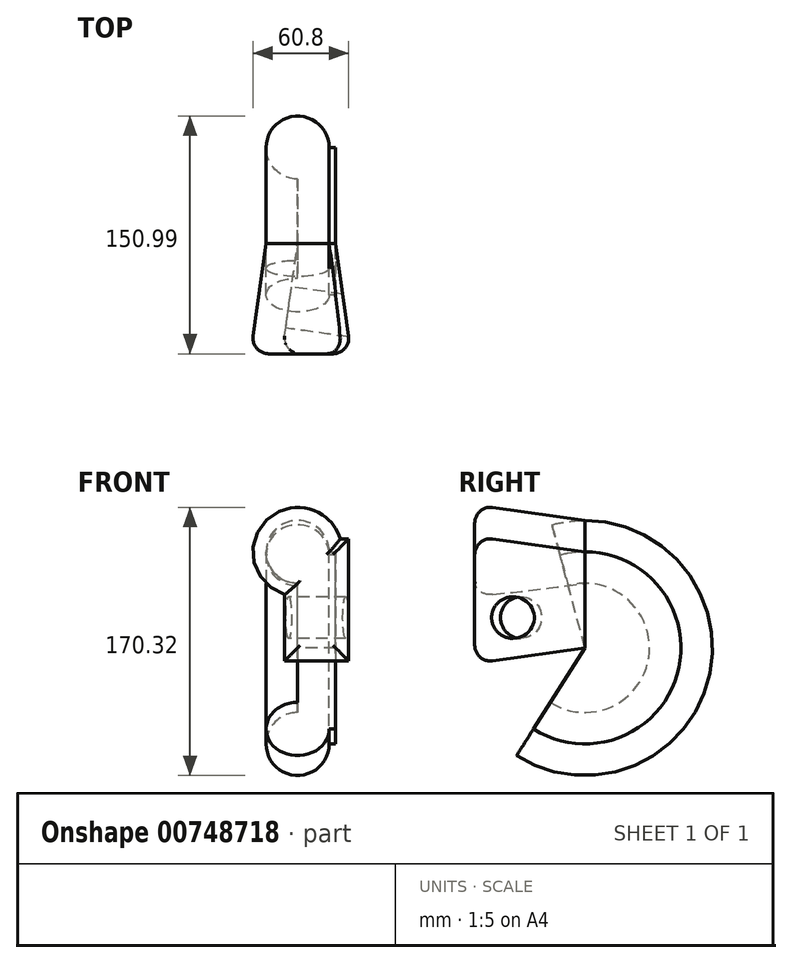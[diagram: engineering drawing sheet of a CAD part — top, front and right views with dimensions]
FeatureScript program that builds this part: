
annotation { "Feature Type Name" : "Feature", "Feature Type Description" : "" }
export const myFeature = defineFeature(function(context is Context, id is Id, definition is map)
    precondition{}
    {
        {
            var Q0;
            Q0=qCreatedBy(makeId("Front.planeOp"),FACE);
            var sketch = newSketch(context, id + "F0", { "sketchPlane" : qUnion([Q0])});
            skArc(sketch, "E0", {"start": v(32.5, -30.94) * mm, "mid": v(-1.64, -16.8) * mm, "end": v(12.5, -50.94) * mm});
            skLineSegment(sketch, "E1.bottom", {"start": v(36.64, -91.93) * mm, "end": v(12.5, -91.93) * mm});
            skLineSegment(sketch, "E1.top", {"start": v(36.64, -30.94) * mm, "end": v(32.5, -30.94) * mm});
            skLineSegment(sketch, "E1.left", {"start": v(36.64, -91.93) * mm, "end": v(36.64, -30.94) * mm});
            skLineSegment(sketch, "E1.right", {"start": v(12.5, -91.93) * mm, "end": v(12.5, -50.94) * mm});
            skSolve(sketch);
        }
        {
            var Q0;
            Q0=makeQuery(id+"F0.imprint","IMPRINT",FACE,{"disambiguationData":[TD([[makeQuery(id+"F0.imprint","IMPRINT",EDGE,{"derivedFrom":sQuery(id+"F0.wireOp",EDGE,"E0")}),1.0]])]});
            extrude(context, id + "F1", {"entities" : qUnion([Q0]), "depth" : 70 * mm, "offsetDistance" : 25 * mm, "hasDraft" : true, "draftAngle" : 8 * degree});
        }
        {
            var Q0;
            Q0 = qSketchRegion(id + "F0", true);
            var Q1;
            Q1=makeQuery(id+"F1.opExtrude","CAP_EDGE",EDGE,{"disambiguationData":[OSD([sQuery(id+"F0.wireOp",EDGE,"E1.bottom")])],"isStart":true});
            revolve(context, id + "F2", {"surfaceOperationType" : NewSurfaceOperationType.NEW, "entities" : qUnion([Q0]), "axis" : qUnion([Q1]), "revolveType" : RevolveType.TWO_DIRECTIONS, "angle" : 212.4 * degree, "angleBack" : 345 * degree});
        }
        {
            var Q0;
            Q0=makeQuery(id+"F1.opExtrude","SWEPT_FACE",FACE,{"disambiguationData":[OSD([sQuery(id+"F0.wireOp",EDGE,"E1.right")])]});
            var sketch = newSketch(context, id + "F3", { "sketchPlane" : qUnion([Q0])});
            skCircle(sketch, "E2", {"center": v(39.23, -72.67) * mm, "radius": 13.2 * mm});
            skSolve(sketch);
        }
        {
            var Q0;
            Q0 = qSketchRegion(id + "F3", true);
            extrude(context, id + "F4", {"entities" : qUnion([Q0]), "operationType" : NewBodyOperationType.REMOVE, "oppositeDirection" : true, "depth" : 89 * mm, "offsetDistance" : 25 * mm});
        }
        {
            var Q0;
            Q0=makeQuery(id+"F1.opExtrude","CAP_EDGE",EDGE,{"disambiguationData":[OSD([sQuery(id+"F0.wireOp",EDGE,"E0")])],"isStart":false});
            var Q1;
            Q1=makeQuery(id+"F1.opExtrude","CAP_EDGE",EDGE,{"disambiguationData":[OSD([sQuery(id+"F0.wireOp",EDGE,"E1.right")])],"isStart":false});
            var Q2;
            Q2=makeQuery(id+"F1.opExtrude","CAP_FACE",FACE,{"disambiguationData":[OSD([sQuery(id+"F0.wireOp",EDGE,"E0"),sQuery(id+"F0.wireOp",EDGE,"E1.bottom"),sQuery(id+"F0.wireOp",EDGE,"E1.top"),sQuery(id+"F0.wireOp",EDGE,"E1.left"),sQuery(id+"F0.wireOp",EDGE,"E1.right")])],"isStart":false});
            fillet(context, id + "F5", {"entities" : qUnion([Q0, Q1, Q2]), "radius" : 10 * mm, "tangentPropagation" : true, "allowEdgeOverflow" : false});
        }
    });
